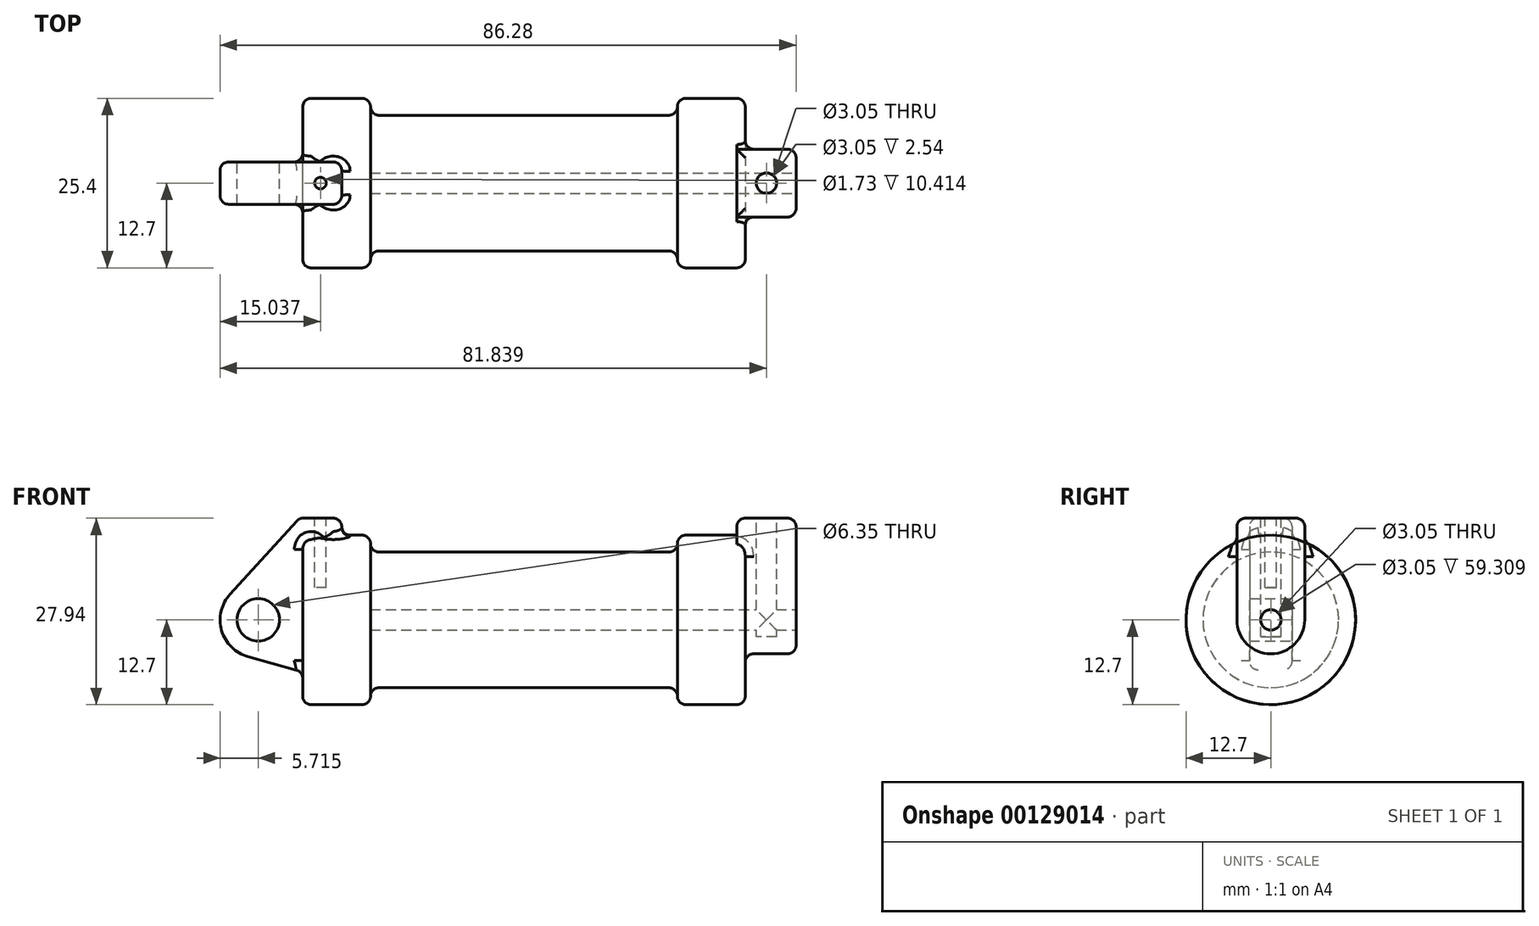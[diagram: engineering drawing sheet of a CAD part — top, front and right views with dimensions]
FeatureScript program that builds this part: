
annotation { "Feature Type Name" : "Feature", "Feature Type Description" : "" }
export const myFeature = defineFeature(function(context is Context, id is Id, definition is map)
    precondition{}
    {
        {
            var Q0;
            Q0=qCreatedBy(makeId("Front.planeOp"),FACE);
            var sketch = newSketch(context, id + "F0", { "sketchPlane" : qUnion([Q0])});
            skLineSegment(sketch, "E0", {"start": v(0, 0) * mm, "end": v(0, 12.7) * mm});
            skLineSegment(sketch, "E1", {"start": v(0, 12.7) * mm, "end": v(10.16, 12.7) * mm});
            skLineSegment(sketch, "E2", {"start": v(10.16, 12.7) * mm, "end": v(10.16, 10.16) * mm});
            skLineSegment(sketch, "E3", {"start": v(10.16, 10.16) * mm, "end": v(56.13, 10.16) * mm});
            skLineSegment(sketch, "E4", {"start": v(56.13, 10.16) * mm, "end": v(56.13, 12.7) * mm});
            skLineSegment(sketch, "E5", {"start": v(56.13, 12.7) * mm, "end": v(66.3, 12.7) * mm});
            skLineSegment(sketch, "E6", {"start": v(66.3, 12.7) * mm, "end": v(66.3, 0) * mm});
            skLineSegment(sketch, "E7", {"start": v(66.3, 0) * mm, "end": v(0, 0) * mm});
            skLineSegment(sketch, "E8", {"start": v(5.84, 15.24) * mm, "end": v(-0.5, 15.24) * mm});
            skLineSegment(sketch, "E9", {"start": v(-0.5, 15.24) * mm, "end": v(-10.88, 3.85) * mm});
            skLineSegment(sketch, "E10", {"start": v(0, 0) * mm, "end": v(-6.65, 0) * mm});
            skCircle(sketch, "E11", {"center": v(-6.65, 0) * mm, "radius": 5.72 * mm});
            skCircle(sketch, "E12", {"center": v(-6.65, 0) * mm, "radius": 3.18 * mm});
            skLineSegment(sketch, "E13", {"start": v(5.84, 15.24) * mm, "end": v(5.84, -9.4) * mm});
            skLineSegment(sketch, "E14", {"start": v(5.84, -9.4) * mm, "end": v(-8.18, -5.5) * mm});
            skSolve(sketch);
        }
        {
            var Q0;
            {var subQ0=sQuery(id+"F0.wireOp",EDGE,"E0");Q0=makeQuery(id+"F0.imprint","IMPRINT",FACE,{"disambiguationData":[TD([[makeQuery(id+"F0.imprint","IMPRINT",EDGE,{"derivedFrom":subQ0}),-1.0]])]});}
            var Q1;
            {var subQ0=sQuery(id+"F0.wireOp",EDGE,"E2");Q1=makeQuery(id+"F0.imprint","IMPRINT",FACE,{"disambiguationData":[TD([[makeQuery(id+"F0.imprint","IMPRINT",EDGE,{"derivedFrom":subQ0}),-1.0]])]});}
            var Q2;
            Q2=sQuery(id+"F0.wireOp",EDGE,"E7");
            revolve(context, id + "F1", {"entities" : qUnion([Q0, Q1]), "axis" : qUnion([Q2]), "revolveType" : RevolveType.FULL});
        }
        {
            var Q0;
            {var subQ4=sQuery(id+"F0.wireOp",EDGE,"E12");Q0=makeQuery(id+"F0.imprint","IMPRINT",FACE,{"disambiguationData":[TD([[makeQuery(id+"F0.imprint","IMPRINT",EDGE,{"derivedFrom":subQ4}),-1.0]])]});}
            var Q1;
            {var subQ3=sQuery(id+"F0.wireOp",EDGE,"E0");Q1=makeQuery(id+"F0.imprint","IMPRINT",FACE,{"disambiguationData":[TD([[makeQuery(id+"F0.imprint","IMPRINT",EDGE,{"derivedFrom":subQ3}),1.0]])]});}
            var Q2;
            {var subQ0=sQuery(id+"F0.wireOp",EDGE,"E14");Q2=makeQuery(id+"F0.imprint","IMPRINT",FACE,{"disambiguationData":[TD([[makeQuery(id+"F0.imprint","IMPRINT",EDGE,{"derivedFrom":subQ0}),-1.0]])]});}
            var Q3;
            {var subQ0=sQuery(id+"F0.wireOp",EDGE,"E0");Q3=makeQuery(id+"F0.imprint","IMPRINT",FACE,{"disambiguationData":[TD([[makeQuery(id+"F0.imprint","IMPRINT",EDGE,{"derivedFrom":subQ0}),-1.0]])]});}
            extrude(context, id + "F2", {"entities" : qUnion([Q0, Q1, Q2, Q3]), "operationType" : NewBodyOperationType.ADD, "endBound" : BoundingType.SYMMETRIC, "depth" : 6.35 * mm, "offsetDistance" : 25.4 * mm});
        }
        {
            var Q0;
            Q0=makeQuery(id+"F1.opRevolve","SWEPT_FACE",FACE,{"disambiguationData":[OSD([sQuery(id+"F0.wireOp",EDGE,"E6")])]});
            var sketch = newSketch(context, id + "F3", { "sketchPlane" : qUnion([Q0])});
            skCircle(sketch, "E15", {"center": v(0, 0) * mm, "radius": 1.52 * mm});
            skCircle(sketch, "E16", {"center": v(0, 0) * mm, "radius": 5.08 * mm});
            skLineSegment(sketch, "E17", {"start": v(-5.08, 0) * mm, "end": v(-5.08, 15.24) * mm});
            skLineSegment(sketch, "E18", {"start": v(-5.08, 15.24) * mm, "end": v(5.08, 15.24) * mm});
            skLineSegment(sketch, "E19", {"start": v(5.08, 15.24) * mm, "end": v(5.08, 0) * mm});
            skSolve(sketch);
        }
        {
            var Q0;
            {var subQ0=sQuery(id+"F3.wireOp",EDGE,"E18");Q0=makeQuery(id+"F3.imprint","IMPRINT",FACE,{"disambiguationData":[TD([[makeQuery(id+"F3.imprint","IMPRINT",EDGE,{"derivedFrom":subQ0}),-1.0]])]});}
            var Q1;
            {var subQ0=sQuery(id+"F3.wireOp",EDGE,"E17");var subQ1=sQuery(id+"F3.wireOp",EDGE,"E16");var subQ2=makeQuery(id+"F3.imprint","INTERSECT",VERTEX,{"derivedFrom":[subQ1,subQ0]});Q1=makeQuery(id+"F3.imprint","IMPRINT",FACE,{"disambiguationData":[TD([[makeQuery(id+"F3.imprint","IMPRINT",EDGE,{"disambiguationData":[TD([[subQ2,1.0]])],"derivedFrom":subQ1}),-1.0]])]});}
            var Q2;
            Q2=makeQuery(id+"F3.imprint","IMPRINT",FACE,{"disambiguationData":[TD([[makeQuery(id+"F3.imprint","IMPRINT",EDGE,{"derivedFrom":sQuery(id+"F3.wireOp",EDGE,"E15")}),-1.0]])]});
            var Q3;
            Q3=sQuery(id+"F3.wireOp",EDGE,"E18");
            var Q4;
            Q4=sQuery(id+"F3.wireOp",EDGE,"E16");
            var Q5;
            Q5=sQuery(id+"F3.wireOp",EDGE,"E19");
            var Q6;
            Q6=sQuery(id+"F3.wireOp",EDGE,"E17");
            var Q7;
            Q7=sQuery(id+"F3.wireOp",EDGE,"E15");
            extrude(context, id + "F4", {"entities" : qUnion([Q0, Q1, Q2]), "operationType" : NewBodyOperationType.ADD, "surfaceEntities" : qUnion([Q3, Q4, Q5, Q6, Q7]), "oppositeDirection" : true, "depth" : 1.27 * mm, "hasSecondDirection" : true, "secondDirectionOppositeDirection" : false, "secondDirectionDepth" : 7.62 * mm});
        }
        {
            var Q0;
            Q0=makeQuery(id+"F2.opExtrude","SWEPT_FACE",FACE,{"disambiguationData":[OSD([sQuery(id+"F0.wireOp",EDGE,"E8")])]});
            var sketch = newSketch(context, id + "F5", { "sketchPlane" : qUnion([Q0])});
            skCircle(sketch, "E20", {"center": v(2.67, 0) * mm, "radius": 0.86 * mm});
            skLineSegment(sketch, "E21", {"start": v(-0.5, 0) * mm, "end": v(5.84, 0) * mm});
            skSolve(sketch);
        }
        {
            var Q0;
            Q0=makeQuery(id+"F4.opExtrude","SWEPT_FACE",FACE,{"disambiguationData":[OSD([sQuery(id+"F3.wireOp",EDGE,"E18")])]});
            var sketch = newSketch(context, id + "F6", { "sketchPlane" : qUnion([Q0])});
            skLineSegment(sketch, "E22", {"start": v(65.02, 0) * mm, "end": v(73.91, 0) * mm});
            skCircle(sketch, "E23", {"center": v(69.47, 0) * mm, "radius": 1.52 * mm});
            skSolve(sketch);
        }
        {
            var Q0;
            {var subQ0=sQuery(id+"F6.wireOp",EDGE,"E23");var subQ1=sQuery(id+"F6.wireOp",EDGE,"E22");var subQ2=makeQuery(id+"F6.imprint","INTERSECT",VERTEX,{"disambiguationData":[OD(0.0)],"derivedFrom":[subQ1,subQ0]});Q0=makeQuery(id+"F6.imprint","IMPRINT",FACE,{"disambiguationData":[TD([[makeQuery(id+"F6.imprint","IMPRINT",EDGE,{"disambiguationData":[TD([[subQ2,-1.0]])],"derivedFrom":subQ1}),-1.0]])]});}
            var Q1;
            {var subQ0=sQuery(id+"F6.wireOp",EDGE,"E23");var subQ1=sQuery(id+"F6.wireOp",EDGE,"E22");var subQ2=makeQuery(id+"F6.imprint","INTERSECT",VERTEX,{"disambiguationData":[OD(0.0)],"derivedFrom":[subQ1,subQ0]});Q1=makeQuery(id+"F6.imprint","IMPRINT",FACE,{"disambiguationData":[TD([[makeQuery(id+"F6.imprint","IMPRINT",EDGE,{"disambiguationData":[TD([[subQ2,-1.0]])],"derivedFrom":subQ1}),1.0]])]});}
            var Q2;
            Q2=sQuery(id+"F6.wireOp",EDGE,"E23");
            extrude(context, id + "F7", {"entities" : qUnion([Q0, Q1]), "operationType" : NewBodyOperationType.REMOVE, "surfaceEntities" : qUnion([Q2]), "oppositeDirection" : true, "depth" : 17.78 * mm});
        }
        {
            var Q0;
            {var subQ0=sQuery(id+"F5.wireOp",EDGE,"E21");var subQ1=sQuery(id+"F5.wireOp",EDGE,"E20");var subQ2=makeQuery(id+"F5.imprint","INTERSECT",VERTEX,{"disambiguationData":[OD(0.0)],"derivedFrom":[subQ1,subQ0]});Q0=makeQuery(id+"F5.imprint","IMPRINT",FACE,{"disambiguationData":[TD([[makeQuery(id+"F5.imprint","IMPRINT",EDGE,{"disambiguationData":[TD([[subQ2,1.0]])],"derivedFrom":subQ1}),1.0]])]});}
            var Q1;
            {var subQ0=sQuery(id+"F5.wireOp",EDGE,"E21");var subQ1=sQuery(id+"F5.wireOp",EDGE,"E20");var subQ2=makeQuery(id+"F5.imprint","INTERSECT",VERTEX,{"disambiguationData":[OD(0.0)],"derivedFrom":[subQ1,subQ0]});Q1=makeQuery(id+"F5.imprint","IMPRINT",FACE,{"disambiguationData":[TD([[makeQuery(id+"F5.imprint","IMPRINT",EDGE,{"disambiguationData":[TD([[subQ2,-1.0]])],"derivedFrom":subQ1}),1.0]])]});}
            extrude(context, id + "F8", {"entities" : qUnion([Q0, Q1]), "operationType" : NewBodyOperationType.REMOVE, "oppositeDirection" : true, "depth" : 10.4 * mm});
        }
        {
            var Q0;
            Q0=makeQuery(id+"F4.opExtrude","CAP_FACE",FACE,{"disambiguationData":[OSD([sQuery(id+"F3.wireOp",EDGE,"E15"),sQuery(id+"F3.wireOp",EDGE,"E16"),sQuery(id+"F3.wireOp",EDGE,"E17"),sQuery(id+"F3.wireOp",EDGE,"E18"),sQuery(id+"F3.wireOp",EDGE,"E19")])],"isStart":true});
            var sketch = newSketch(context, id + "F9", { "sketchPlane" : qUnion([Q0])});
            skLineSegment(sketch, "E24", {"start": v(-1.52, 0) * mm, "end": v(1.52, 0) * mm});
            skSolve(sketch);
        }
        {
            var Q0;
            {var subQ0=sQuery(id+"F9.wireOp",EDGE,"E24");Q0=makeQuery(id+"F9.imprint","IMPRINT",FACE,{"disambiguationData":[TD([[makeQuery(id+"F9.imprint","IMPRINT",EDGE,{"derivedFrom":subQ0}),1.0]])]});}
            var Q1;
            {var subQ0=sQuery(id+"F9.wireOp",EDGE,"E24");Q1=makeQuery(id+"F9.imprint","IMPRINT",FACE,{"disambiguationData":[TD([[makeQuery(id+"F9.imprint","IMPRINT",EDGE,{"derivedFrom":subQ0}),-1.0]])]});}
            var Q2;
            Q2=makeQuery(id+"F1.opRevolve","SWEPT_FACE",FACE,{"disambiguationData":[OSD([sQuery(id+"F0.wireOp",EDGE,"E2")])]});
            extrude(context, id + "F10", {"entities" : qUnion([Q0, Q1]), "operationType" : NewBodyOperationType.REMOVE, "endBound" : BoundingType.UP_TO_SURFACE, "oppositeDirection" : true, "endBoundEntityFace" : qUnion([Q2]), "depth" : 25.4 * mm});
        }
        {
            var Q0;
            Q0=makeQuery(id+"F4.boolean.opBoolean","SPLIT",FACE,{"disambiguationData":[TD([makeQuery(id+"F1.opRevolve","SWEPT_FACE",FACE,{"disambiguationData":[OSD([sQuery(id+"F0.wireOp",EDGE,"E5")])]})])],"derivedFrom":makeQuery(id+"F1.opRevolve","SWEPT_FACE",FACE,{"disambiguationData":[OSD([sQuery(id+"F0.wireOp",EDGE,"E6")])]})});
            var Q1;
            Q1=makeQuery(id+"F1.opRevolve","SWEPT_FACE",FACE,{"disambiguationData":[OSD([sQuery(id+"F0.wireOp",EDGE,"E2")])]});
            var Q2;
            Q2=makeQuery(id+"F1.opRevolve","SWEPT_FACE",FACE,{"disambiguationData":[OSD([sQuery(id+"F0.wireOp",EDGE,"E4")])]});
            var Q3;
            Q3=makeQuery(id+"F1.opRevolve","SWEPT_FACE",FACE,{"disambiguationData":[OSD([sQuery(id+"F0.wireOp",EDGE,"E0")])]});
            var Q4;
            Q4=makeQuery(id+"F4.opExtrude","CAP_EDGE",EDGE,{"disambiguationData":[OSD([sQuery(id+"F3.wireOp",EDGE,"E19")])],"isStart":true});
            var Q5;
            Q5=makeQuery(id+"F4.opExtrude","CAP_EDGE",EDGE,{"disambiguationData":[OSD([sQuery(id+"F3.wireOp",EDGE,"E18")])],"isStart":true});
            var Q6;
            Q6=makeQuery(id+"F4.opExtrude","SWEPT_EDGE",EDGE,{"disambiguationData":[OSD([sQuery(id+"F3.wireOp",EDGE,"E18"),sQuery(id+"F3.wireOp",EDGE,"E19")])]});
            var Q7;
            Q7=makeQuery(id+"F4.opExtrude","CAP_EDGE",EDGE,{"disambiguationData":[OSD([sQuery(id+"F3.wireOp",EDGE,"E18")])],"isStart":false});
            var Q8;
            Q8=makeQuery(id+"F4.opExtrude","SWEPT_EDGE",EDGE,{"disambiguationData":[OSD([sQuery(id+"F3.wireOp",EDGE,"E17"),sQuery(id+"F3.wireOp",EDGE,"E18")])]});
            var Q9;
            Q9=makeQuery(id+"F2.opExtrude","CAP_EDGE",EDGE,{"disambiguationData":[OSD([sQuery(id+"F0.wireOp",EDGE,"E8")])],"isStart":false});
            var Q10;
            Q10=makeQuery(id+"F2.opExtrude","SWEPT_EDGE",EDGE,{"disambiguationData":[OSD([sQuery(id+"F0.wireOp",EDGE,"E8"),sQuery(id+"F0.wireOp",EDGE,"E9")])]});
            var Q11;
            Q11=makeQuery(id+"F2.opExtrude","CAP_EDGE",EDGE,{"disambiguationData":[OSD([sQuery(id+"F0.wireOp",EDGE,"E9")])],"isStart":true});
            var Q12;
            Q12=makeQuery(id+"F2.opExtrude","CAP_EDGE",EDGE,{"disambiguationData":[OSD([sQuery(id+"F0.wireOp",EDGE,"E9")])],"isStart":false});
            var Q13;
            Q13=makeQuery(id+"F2.opExtrude","SWEPT_FACE",FACE,{"disambiguationData":[OSD([sQuery(id+"F0.wireOp",EDGE,"E11")])]});
            var Q14;
            Q14=makeQuery(id+"F2.opExtrude","SWEPT_EDGE",EDGE,{"disambiguationData":[OSD([sQuery(id+"F0.wireOp",EDGE,"E8"),sQuery(id+"F0.wireOp",EDGE,"E13")])]});
            var Q15;
            Q15=makeQuery(id+"F2.opExtrude","CAP_EDGE",EDGE,{"disambiguationData":[OSD([sQuery(id+"F0.wireOp",EDGE,"E8")])],"isStart":true});
            fillet(context, id + "F11", {"entities" : qUnion([Q0, Q1, Q2, Q3, Q4, Q5, Q6, Q7, Q8, Q9, Q10, Q11, Q12, Q13, Q14, Q15]), "radius" : 1.27 * mm, "tangentPropagation" : true, "allowEdgeOverflow" : false});
        }
        {
            var Q0;
            Q0=makeQuery(id+"F2.opExtrude","SWEPT_FACE",FACE,{"disambiguationData":[OSD([sQuery(id+"F0.wireOp",EDGE,"E13")])]});
            var Q1;
            Q1=makeQuery(id+"F1.opRevolve","SWEPT_FACE",FACE,{"disambiguationData":[OSD([sQuery(id+"F0.wireOp",EDGE,"E0")])]});
            fillet(context, id + "F12", {"entities" : qUnion([Q0, Q1]), "radius" : 1.27 * mm, "tangentPropagation" : true, "allowEdgeOverflow" : false});
        }
    });
